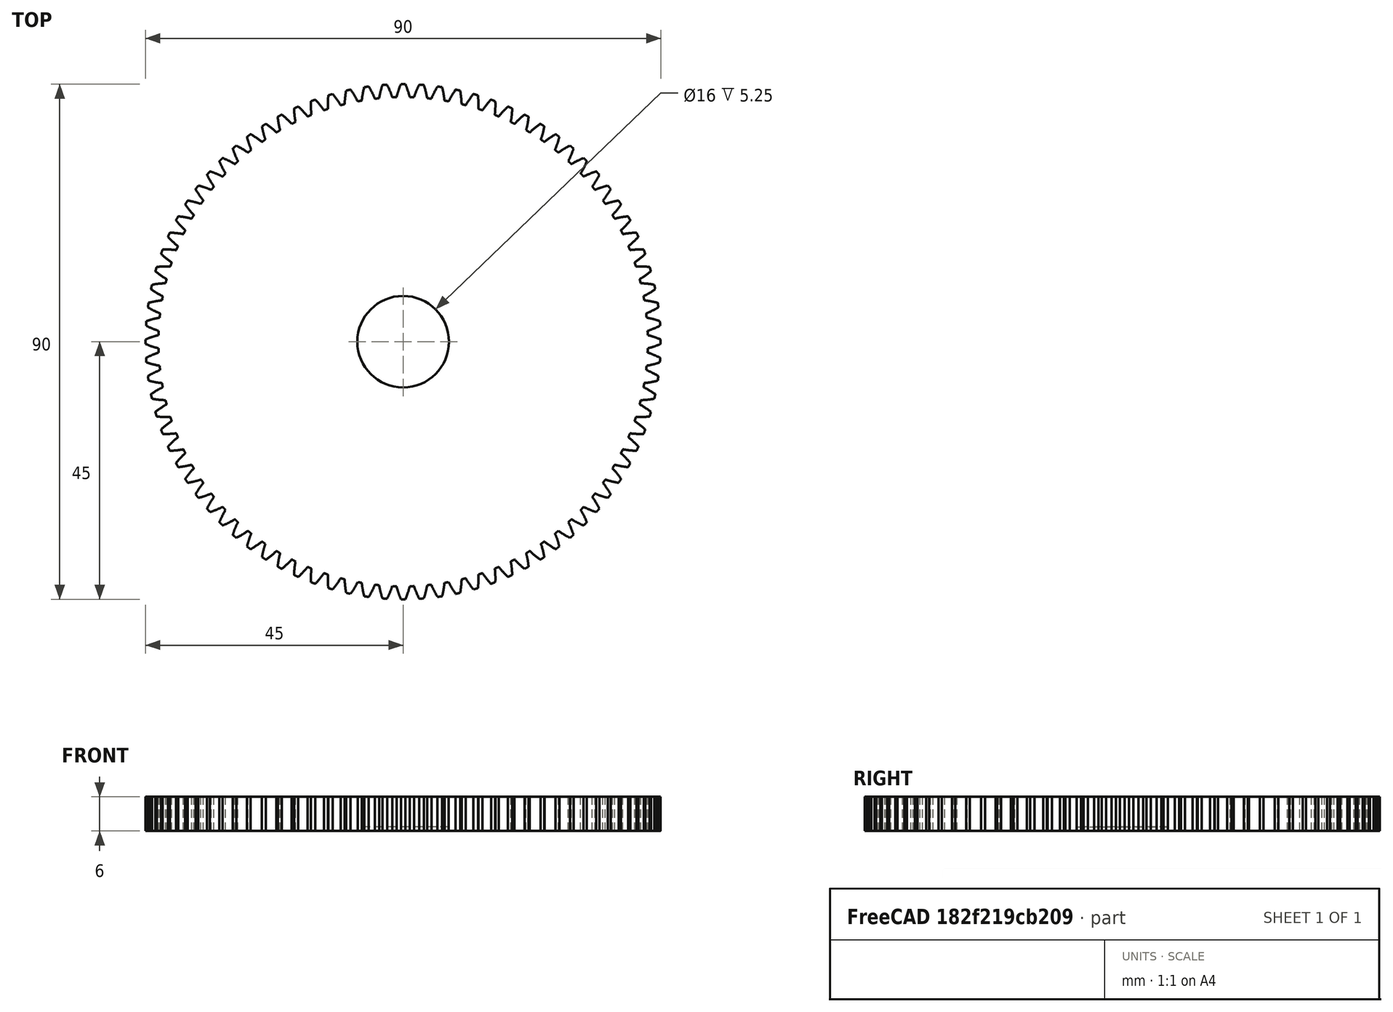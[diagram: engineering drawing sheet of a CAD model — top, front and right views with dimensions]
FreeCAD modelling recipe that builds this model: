
FCSTD DOCUMENT  (FreeCAD 0.19R)
Label: c-axis-turntable
License: All rights reserved
LicenseURL: http://en.wikipedia.org/wiki/All_rights_reserved
objects: PartDesign::FeaturePython×1, Sketcher::SketchObject×1, PartDesign::Pocket×1, PartDesign::Body×1
note: 5 computed .brp shape members not serialized (recipe doc carries the construction recipe); baked Part::Feature solids carry a one-line shape summary decoded from their .brp

FEATURE [PartDesign::FeaturePython] involutegear  # WARN: FeaturePython — macro-defined, semantics opaque (R4)
  AttacherType = Attacher::AttachEngine3D
  backlash = 0
  beta = 0
  clearance = 0.25
  da = 90
  df = 85.5
  double_helix = false
  dw = 88
  head = 0
  height = 6
  module = 1
  numpoints = 6
  pressure_angle = 20
  properties_from_tool = false
  reversed_backlash = false
  shift = 0
  simple = false
  teeth = 88
  transverse_pitch = 3.14159
  undercut = false
  version = 0.0.3
FEATURE [Sketcher::SketchObject] Sketch
  FullyConstrained = true
  MapMode = 5
  Placement = pos=(0,0,6) rot=(0,0,1;0rad)
  Support = -> [involutegear]
  sketch-geometry (1):
    g0: Circle CenterX=0 CenterY=0 CenterZ=0 NormalX=0 NormalY=0 NormalZ=1 AngleXU=0 Radius=8
  constraints (2):
    c: Coincident(g0,g-1)
    c: Diameter(g0) = 16
FEATURE [PartDesign::Pocket] Pocket
  BaseFeature = -> involutegear
  Length = 5.25
  Length2 = 100
  Profile = -> Sketch
  Type = 0
FEATURE [PartDesign::Body] Body
  Group = -> [involutegear,Sketch,Pocket]
  Origin = -> Origin
  Tip = -> Pocket
